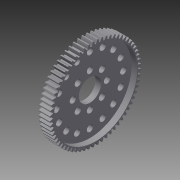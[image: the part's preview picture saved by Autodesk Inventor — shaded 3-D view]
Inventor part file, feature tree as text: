
AUTODESK INVENTOR PART (.ipt)
format: ipt  version: 2015 (Build 190159000, 159)  size: 866,816 bytes
history: native  units: in
note: dims shown in document units (in); Inventor stores cm internally (conversion verified against a paired STEP export)
features: other x3, sketch x2, extrude x2, hole x1
ambient origin geometry x8: Origin, YZ Plane, XZ Plane, XY Plane, X Axis, Y Axis, Z Axis, Center Point
bodies: Solid1 (feature_tree)
feature tree (8):
  other  "User Library-6151941"
  sketch  "Sketch2"  dims[d11=0.5in d13=0.1406in]
  extrude  "Extrusion2"  Depth=0.1406in
  extrude  "Extrusion3"  Depth=0.25in
  hole  "Hole1"  [1 undecoded]
  sketch  "Sketch3"  dims[d14=0.1406in d16=1.0315in d17=1.5748in d19=360.0deg d21=1.5in d22=1.875in d23=3.1496in d25=360.0deg d27=6.2992in d29=360.0deg d31=0.125in d32=0.0in d33=0.4in d34=0.4in d36=0.9605in d37=0.5in d38=1.875in d39=25.1969in d41=360.0deg d43=1.0in d44=0.0in d45=0.14in d46=0.75in d47=0.375in d48=0.25in d49=0.5635in d50=1.0in d51=0.8108in]
  other  "Composite1"
  other  "Srf1"
note: 1 required parameter value undecoded (feature->parameter linkage not recoverable at this tier; creation-order binding heuristic only, values carry confidence <= 0.55)
